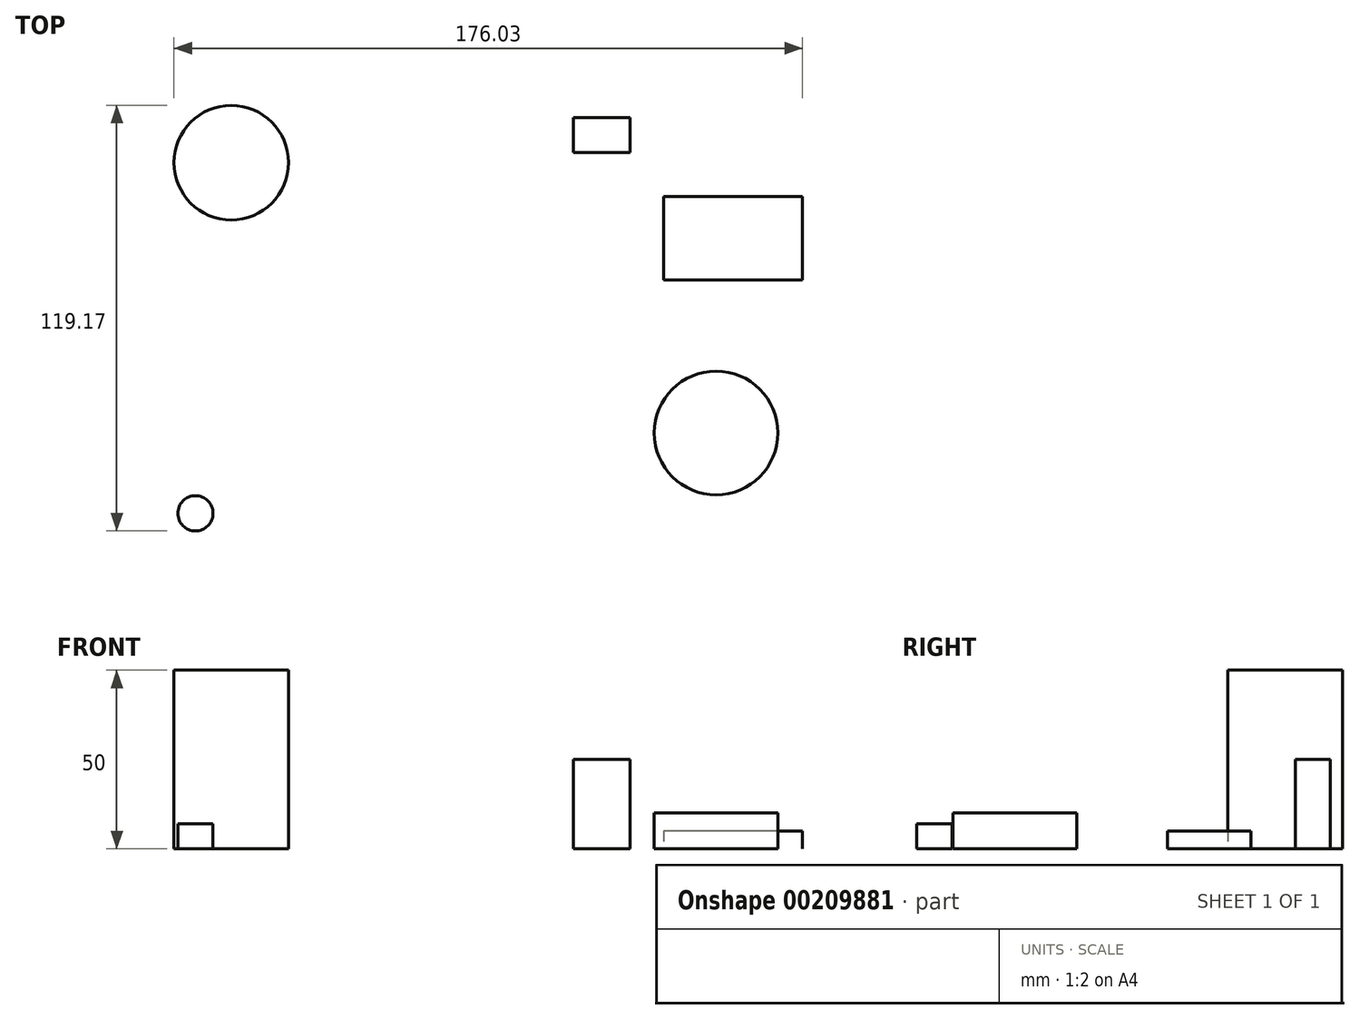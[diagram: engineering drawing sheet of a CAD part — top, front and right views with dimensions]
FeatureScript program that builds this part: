
annotation { "Feature Type Name" : "Feature", "Feature Type Description" : "" }
export const myFeature = defineFeature(function(context is Context, id is Id, definition is map)
    precondition{}
    {
        {
            var Q0;
            Q0=qCreatedBy(makeId("Top.planeOp"),FACE);
            var sketch = newSketch(context, id + "F0", { "sketchPlane" : qUnion([Q0])});
            skCircle(sketch, "E0", {"center": v(0, 0) * mm, "radius": 16.04 * mm});
            skSolve(sketch);
        }
        {
            var Q0;
            Q0=makeQuery(id+"F0.imprint","IMPRINT",FACE,{"disambiguationData":[TD([[makeQuery(id+"F0.imprint","IMPRINT",EDGE,{"derivedFrom":sQuery(id+"F0.wireOp",EDGE,"E0")}),1.0]])]});
            extrude(context, id + "F1", {"entities" : qUnion([Q0]), "depth" : 50 * mm});
        }
        {
            var Q0;
            Q0=qCreatedBy(makeId("Top.planeOp"),FACE);
            var sketch = newSketch(context, id + "F2", { "sketchPlane" : qUnion([Q0])});
            skCircle(sketch, "E1", {"center": v(135.77, -75.7) * mm, "radius": 17.32 * mm});
            skSolve(sketch);
        }
        {
            var Q0;
            Q0=makeQuery(id+"F2.imprint","IMPRINT",FACE,{"disambiguationData":[TD([[makeQuery(id+"F2.imprint","IMPRINT",EDGE,{"derivedFrom":sQuery(id+"F2.wireOp",EDGE,"E1")}),1.0]])]});
            extrude(context, id + "F3", {"entities" : qUnion([Q0]), "depth" : 10 * mm});
        }
        {
            var Q0;
            Q0=qCreatedBy(makeId("Top.planeOp"),FACE);
            var sketch = newSketch(context, id + "F4", { "sketchPlane" : qUnion([Q0])});
            skCircle(sketch, "E2", {"center": v(-10.03, -98.2) * mm, "radius": 4.93 * mm});
            skSolve(sketch);
        }
        {
            var Q0;
            Q0=makeQuery(id+"F4.imprint","IMPRINT",FACE,{"disambiguationData":[TD([[makeQuery(id+"F4.imprint","IMPRINT",EDGE,{"derivedFrom":sQuery(id+"F4.wireOp",EDGE,"E2")}),1.0]])]});
            extrude(context, id + "F5", {"entities" : qUnion([Q0]), "depth" : 7 * mm});
        }
        {
            var Q0;
            Q0=qCreatedBy(makeId("Top.planeOp"),FACE);
            var sketch = newSketch(context, id + "F6", { "sketchPlane" : qUnion([Q0])});
            skLineSegment(sketch, "E3.bottom", {"start": v(160, -9.51) * mm, "end": v(121.06, -9.51) * mm});
            skLineSegment(sketch, "E3.top", {"start": v(160, -32.87) * mm, "end": v(121.06, -32.87) * mm});
            skLineSegment(sketch, "E3.left", {"start": v(160, -9.51) * mm, "end": v(160, -32.87) * mm});
            skLineSegment(sketch, "E3.right", {"start": v(121.06, -9.51) * mm, "end": v(121.06, -32.87) * mm});
            skPoint(sketch, "E3.middle", {"position": v(140.53, -21.2) * mm});
            skSolve(sketch);
        }
        {
            var Q0;
            Q0=makeQuery(id+"F6.imprint","IMPRINT",FACE,{"disambiguationData":[TD([[makeQuery(id+"F6.imprint","IMPRINT",EDGE,{"derivedFrom":sQuery(id+"F6.wireOp",EDGE,"E3.bottom")}),1.0]])]});
            extrude(context, id + "F7", {"entities" : qUnion([Q0]), "depth" : 5 * mm});
        }
        {
            var Q0;
            Q0=qCreatedBy(makeId("Top.planeOp"),FACE);
            var sketch = newSketch(context, id + "F8", { "sketchPlane" : qUnion([Q0])});
            skLineSegment(sketch, "E4.bottom", {"start": v(95.82, 12.65) * mm, "end": v(111.73, 12.65) * mm});
            skLineSegment(sketch, "E4.top", {"start": v(95.82, 2.86) * mm, "end": v(111.73, 2.86) * mm});
            skLineSegment(sketch, "E4.left", {"start": v(95.82, 12.65) * mm, "end": v(95.82, 2.86) * mm});
            skLineSegment(sketch, "E4.right", {"start": v(111.73, 12.65) * mm, "end": v(111.73, 2.86) * mm});
            skPoint(sketch, "E4.middle", {"position": v(103.77, 7.75) * mm});
            skSolve(sketch);
        }
        {
            var Q0;
            Q0=makeQuery(id+"F8.imprint","IMPRINT",FACE,{"disambiguationData":[TD([[makeQuery(id+"F8.imprint","IMPRINT",EDGE,{"derivedFrom":sQuery(id+"F8.wireOp",EDGE,"E4.bottom")}),-1.0]])]});
            extrude(context, id + "F9", {"entities" : qUnion([Q0]), "depth" : 25 * mm});
        }
    });
